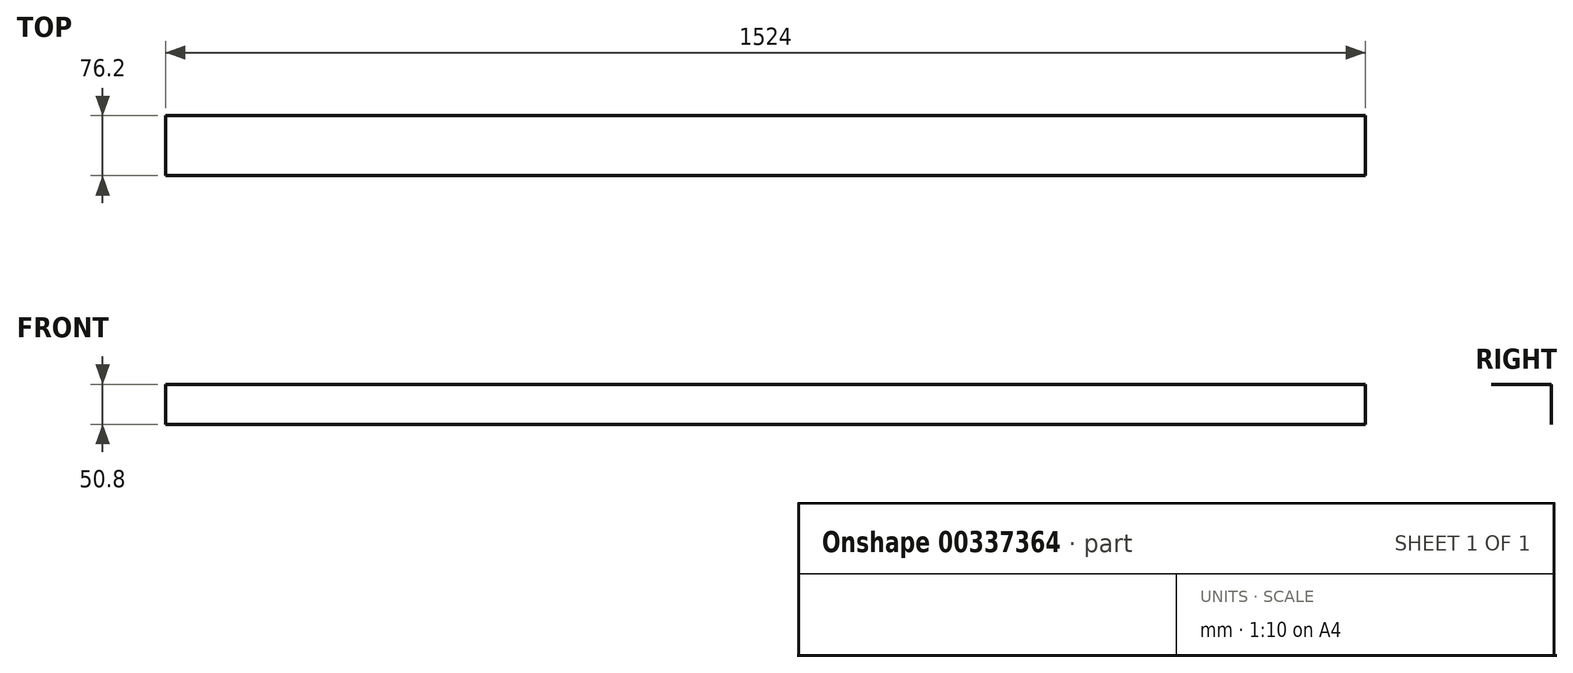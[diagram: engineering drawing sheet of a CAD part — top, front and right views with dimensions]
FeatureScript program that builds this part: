
annotation { "Feature Type Name" : "Feature", "Feature Type Description" : "" }
export const myFeature = defineFeature(function(context is Context, id is Id, definition is map)
    precondition{}
    {
        {
            var Q0;
            Q0=qCreatedBy(makeId("Right.planeOp"),FACE);
            var sketch = newSketch(context, id + "F0", { "sketchPlane" : qUnion([Q0])});
            skLineSegment(sketch, "E0", {"start": v(-25.77, -49.76) * mm, "end": v(-25.77, 1.04) * mm});
            skLineSegment(sketch, "E1", {"start": v(-25.77, 1.04) * mm, "end": v(-101.97, 1.04) * mm});
            skSolve(sketch);
        }
        {
            var Q0;
            Q0 = qSketchRegion(id + "F0", true);
            var Q1;
            Q1=sQuery(id+"F0.wireOp",EDGE,"hjdXlMUY-Jb6S-SjNc-xXW8-q3lcygYq6nEY");
            var Q2;
            Q2=sQuery(id+"F0.wireOp",EDGE,"E0");
            extrude(context, id + "F1", {"entities" : qUnion([Q0]), "bodyType" : ToolBodyType.SURFACE, "surfaceEntities" : qUnion([Q1, Q2]), "depth" : 1524 * mm});
        }
        {
            var Q0;
            Q0 = qSketchRegion(id + "F0", true);
            var Q1;
            Q1=sQuery(id+"F0.wireOp",EDGE,"E1");
            var Q2;
            Q2=sQuery(id+"F0.wireOp",EDGE,"E0");
            extrude(context, id + "F2", {"entities" : qUnion([Q0]), "bodyType" : ToolBodyType.SURFACE, "surfaceEntities" : qUnion([Q1, Q2]), "depth" : 1524 * mm});
        }
    });
